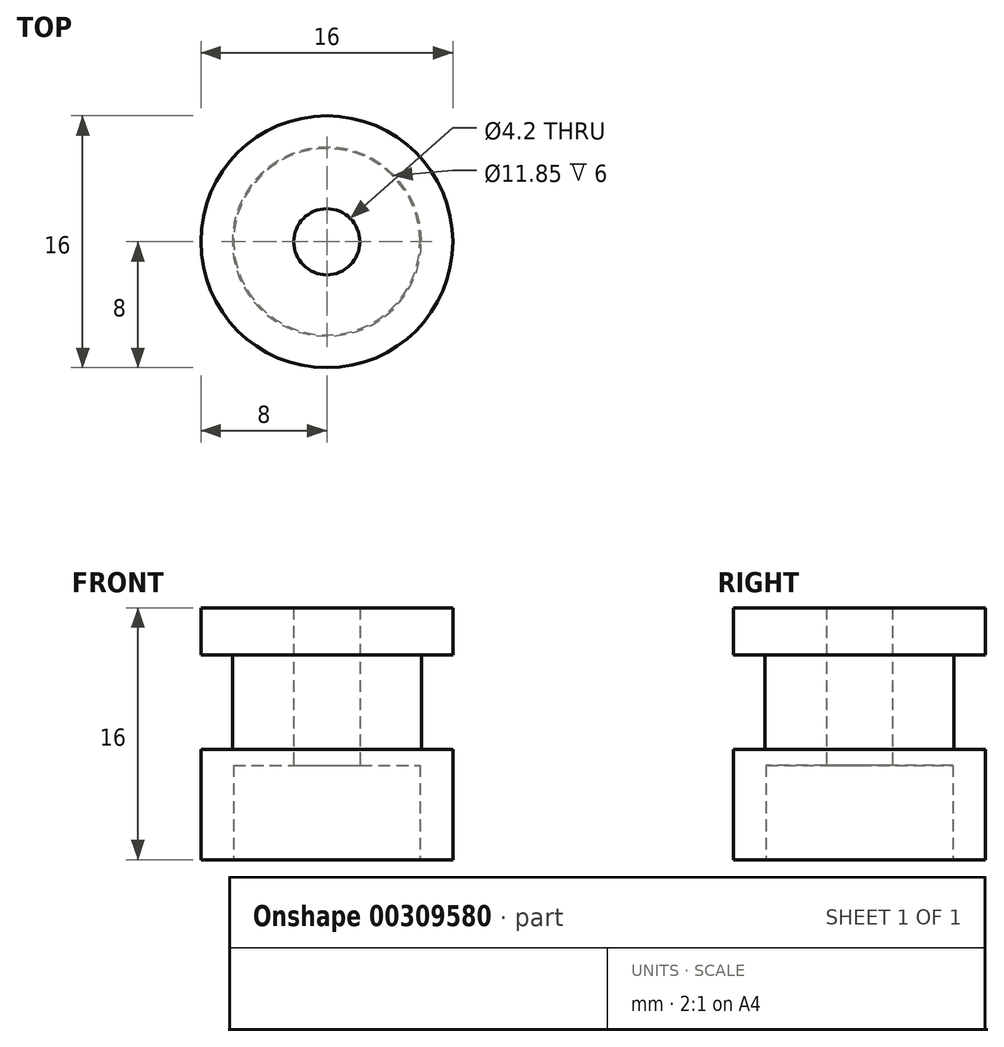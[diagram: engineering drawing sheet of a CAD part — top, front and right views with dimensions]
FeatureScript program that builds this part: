
annotation { "Feature Type Name" : "Feature", "Feature Type Description" : "" }
export const myFeature = defineFeature(function(context is Context, id is Id, definition is map)
    precondition{}
    {
        {
            var Q0;
            Q0=qCreatedBy(makeId("Front.planeOp"),FACE);
            var sketch = newSketch(context, id + "F0", { "sketchPlane" : qUnion([Q0])});
            skLineSegment(sketch, "E0", {"start": v(8, 16) * mm, "end": v(8, 13) * mm});
            skLineSegment(sketch, "E1", {"start": v(6, 13) * mm, "end": v(8, 13) * mm});
            skLineSegment(sketch, "E2", {"start": v(6, 13) * mm, "end": v(6, 7) * mm});
            skLineSegment(sketch, "E3", {"start": v(6, 7) * mm, "end": v(8, 7) * mm});
            skLineSegment(sketch, "E4", {"start": v(8, 7) * mm, "end": v(8, 0) * mm});
            skLineSegment(sketch, "E5", {"start": v(8, 0) * mm, "end": v(0, 0) * mm});
            skLineSegment(sketch, "E6", {"start": v(8, 16) * mm, "end": v(0, 16) * mm});
            skLineSegment(sketch, "E7", {"start": v(0, 0) * mm, "end": v(0, 16) * mm});
            skSolve(sketch);
        }
        {
            var Q0;
            Q0=makeQuery(id+"F0.imprint","IMPRINT",FACE,{"disambiguationData":[TD([[makeQuery(id+"F0.imprint","IMPRINT",EDGE,{"derivedFrom":sQuery(id+"F0.wireOp",EDGE,"E0")}),-1.0]])]});
            var Q1;
            Q1=sQuery(id+"F0.wireOp",EDGE,"E7");
            revolve(context, id + "F1", {"entities" : qUnion([Q0]), "axis" : qUnion([Q1]), "revolveType" : RevolveType.FULL});
        }
        {
            var Q0;
            Q0=makeQuery(id+"F1.opRevolve","SWEPT_FACE",FACE,{"disambiguationData":[OSD([sQuery(id+"F0.wireOp",EDGE,"E5")])]});
            var sketch = newSketch(context, id + "F2", { "sketchPlane" : qUnion([Q0])});
            skCircle(sketch, "E8.0", {"center": v(0, 0) * mm, "radius": 8 * mm});
            skSolve(sketch);
        }
        {
            var Q0;
            Q0=sQuery(id+"F2.wireOp",VERTEX,"E8.0.center");
            var Q1;
            Q1=makeQuery(id+"F1.opRevolve","SWEPT_BODY",BODY,{"disambiguationData":[OSD([sQuery(id+"F0.wireOp",EDGE,"E0"),sQuery(id+"F0.wireOp",EDGE,"E1"),sQuery(id+"F0.wireOp",EDGE,"E2"),sQuery(id+"F0.wireOp",EDGE,"E3"),sQuery(id+"F0.wireOp",EDGE,"E4"),sQuery(id+"F0.wireOp",EDGE,"E5"),sQuery(id+"F0.wireOp",EDGE,"E6"),sQuery(id+"F0.wireOp",EDGE,"E7")])]});
            hole(context, id + "F3", {"style" : HoleStyle.C_BORE, "endStyle" : HoleEndStyle.THROUGH, "holeDiameter" : 4.2 * mm, "cBoreDiameter" : 11.85 * mm, "cBoreDepth" : 6 * mm, "isTappedThrough" : true, "tappedDepth" : 12 * mm, "tapClearance" : 3, "startFromSketch" : true, "locations" : qUnion([Q0]), "scope" : qUnion([Q1])});
        }
    });
